# Revit family: 57_CRD_ME_Climarad_2-0_elektrisch
name_source: partatom
category: Mechanical Equipment
units: mm (PartAtom-declared; Revit-internal decimal feet)

## family parameters
Always vertical = Yes
Classification = None
Cut with Voids When Loaded = Yes
Part Type = Normal
Room Calculation Point = Yes
Round Connector Dimension = Use Diameter
Shared = No
Work Plane-Based = Yes

## types (1)
- 1500 mm
    Default Elevation = 1219 mm
    Description = ClimaRad Sensa H2X ventilatie-unit
    Manufacturer = ClimaRad
    Model = Sensa H2X
    diepte = 245 mm  [stored 0.803806 ft]
    diepte_achterunit = 135 mm  [stored 0.442913 ft]
    diepte_kast = 197 mm
    hart_doorvoer_tov_ok_kast = 367 mm  [stored 1.20407 ft]
    hart_ventilatie_doorvoer_tov_onderkant_unit = 385 mm  [stored 1.26312 ft]
    hoh_ventilatie_doorvoeren = 1098 mm  [stored 3.60236 ft]
    hoogte_kast = 474 mm  [stored 1.55512 ft]
    hoogte_totaal = 554 mm  [stored 1.81759 ft]
    hoogte_unit = 466 mm  [stored 1.52887 ft]
    lengte_kast = 2400 mm
    lengte_onderstel = 700 mm  [stored 2.29659 ft]
    lengte_unit = 1240 mm  [stored 4.06824 ft]
    positie_wcd_uit_hart_unit = 750 mm  [stored 2.46063 ft]
    schacht = Yes
    type_kap = 57_CRD_ME_kap_climarad_2-0 : diepte 197 mm
    voltage = 230 V

note: [stored X ft] marks values corroborated as IEEE doubles in the binary element streams (Revit-internal decimal feet)

## geometry (parser evidence)
native form markers: Sweep x12
no freeform markers — native parametric forms only
